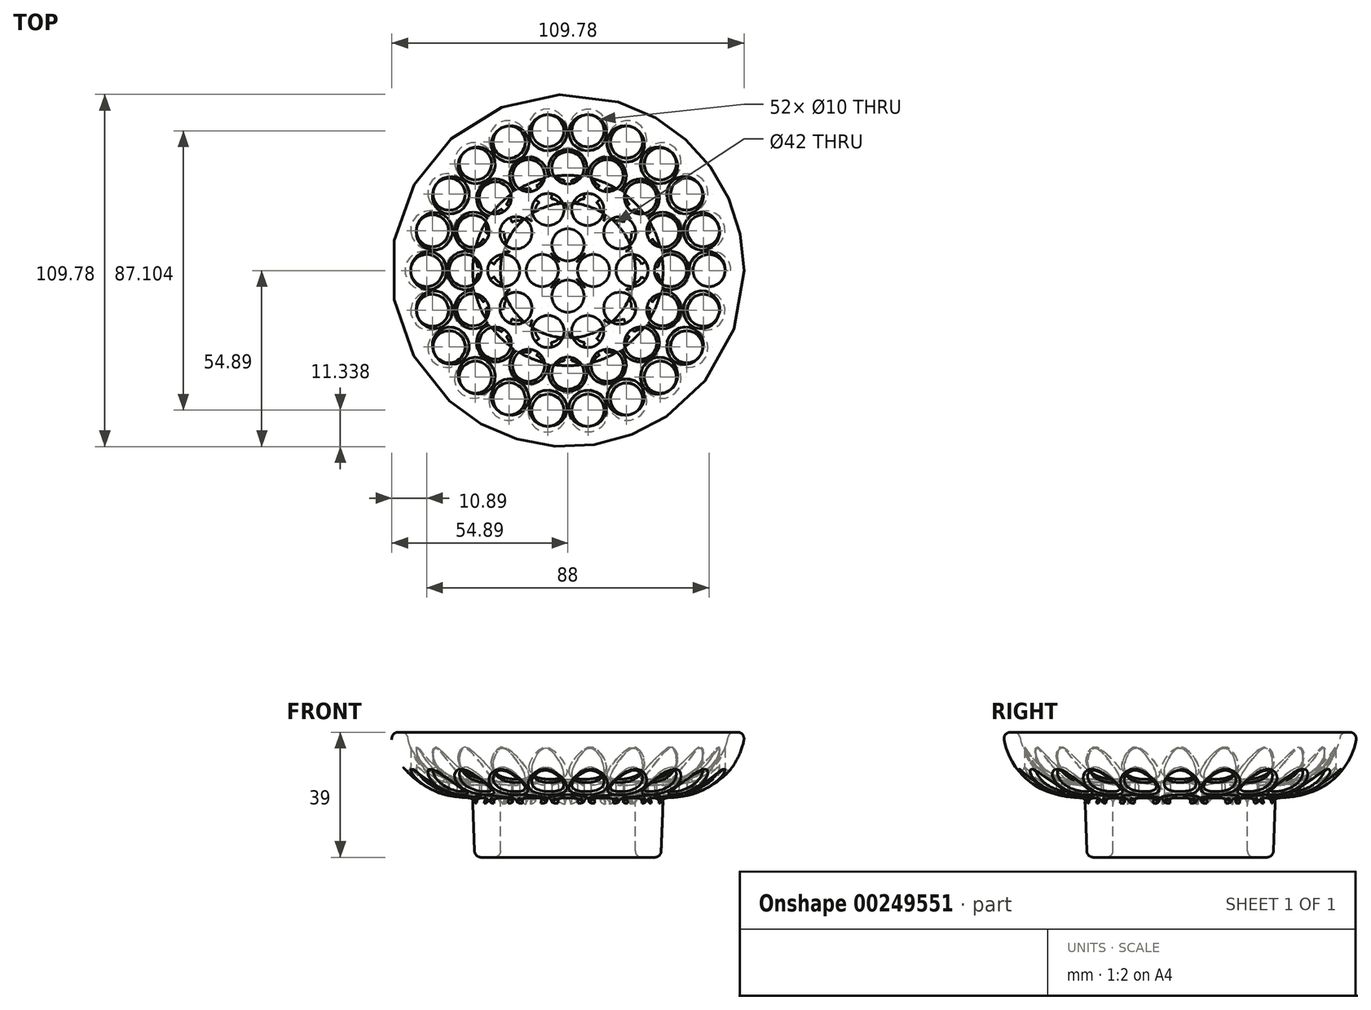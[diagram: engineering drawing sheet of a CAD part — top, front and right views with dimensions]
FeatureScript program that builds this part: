
annotation { "Feature Type Name" : "Feature", "Feature Type Description" : "" }
export const myFeature = defineFeature(function(context is Context, id is Id, definition is map)
    precondition{}
    {
        {
            var Q0;
            Q0=qCreatedBy(makeId("Front.planeOp"),FACE);
            var sketch = newSketch(context, id + "F0", { "sketchPlane" : qUnion([Q0])});
            skLineSegment(sketch, "E0", {"start": v(-23, 0) * mm, "end": v(-27.07, 0) * mm});
            skLineSegment(sketch, "E1", {"start": v(-29.07, 1.92) * mm, "end": v(-29.63, 16.62) * mm});
            skFitSpline(sketch, "E2", {"points": [v(-29.7, 18.5) * mm, v(-54.72, 35.89) * mm, v(-55, 39) * mm], "startDerivative": vector(-74.15, 0) * mm, "endDerivative": vector(0, 6.7) * mm});
            skFitSpline(sketch, "E3.0", {"points": [v(-29.7, 23.5) * mm, v(-32.43, 23.5) * mm, v(-37.07, 24.09) * mm, v(-41.99, 26.08) * mm, v(-45.41, 28.7) * mm, v(-47.75, 31.65) * mm, v(-48.95, 34.1) * mm, v(-49.55, 35.8) * mm, v(-49.78, 36.7) * mm, v(-49.9, 37.26) * mm, v(-49.97, 37.72) * mm, v(-50, 38.13) * mm, v(-50, 38.4) * mm, v(-50, 38.68) * mm, v(-50, 38.88) * mm, v(-50, 39) * mm]});
            skLineSegment(sketch, "E4", {"start": v(-52.89, 39) * mm, "end": v(-51.88, 39) * mm});
            skLineSegment(sketch, "E5", {"start": v(-29.7, 23.5) * mm, "end": v(0, 23.5) * mm});
            skLineSegment(sketch, "E6", {"start": v(0, 23.5) * mm, "end": v(0, 17.86) * mm});
            skLineSegment(sketch, "E7", {"start": v(0, 57.97) * mm, "end": v(0, -37.79) * mm, "construction": true});
            skLineSegment(sketch, "E8", {"start": v(-21, 2) * mm, "end": v(-21, 16.5) * mm});
            skLineSegment(sketch, "E9", {"start": v(-19, 18.5) * mm, "end": v(0, 18.5) * mm});
            skPoint(sketch, "E10.visualSharp", {"position": v(-21, 18.5) * mm});
            skArc(sketch, "E10.filletArc", {"start": v(-19, 18.5) * mm, "mid": v(-20.41, 17.91) * mm, "end": v(-21, 16.5) * mm});
            skPoint(sketch, "E11.visualSharp", {"position": v(-21, 0) * mm});
            skArc(sketch, "E11.filletArc", {"start": v(-23, 0) * mm, "mid": v(-21.59, 0.59) * mm, "end": v(-21, 2) * mm});
            skPoint(sketch, "E12.visualSharp", {"position": v(-29, 0) * mm});
            skArc(sketch, "E12.filletArc", {"start": v(-29.07, 1.92) * mm, "mid": v(-28.46, 0.56) * mm, "end": v(-27.07, 0) * mm});
            skArc(sketch, "E13.filletArc", {"start": v(-29.63, 16.62) * mm, "mid": v(-30.2, 17.95) * mm, "end": v(-31.54, 18.54) * mm});
            skArc(sketch, "E14.filletArc", {"start": v(-52.89, 39) * mm, "mid": v(-54.4, 38.3) * mm, "end": v(-54.87, 36.7) * mm});
            skPoint(sketch, "E15.visualSharp", {"position": v(-50, 39) * mm});
            skArc(sketch, "E15.filletArc", {"start": v(-49.9, 37.34) * mm, "mid": v(-50.59, 38.53) * mm, "end": v(-51.88, 39) * mm});
            skSolve(sketch);
        }
        {
            var Q0;
            Q0=makeQuery(id+"F0.imprint","IMPRINT",FACE,{"disambiguationData":[TD([[makeQuery(id+"F0.imprint","IMPRINT",EDGE,{"derivedFrom":sQuery(id+"F0.wireOp",EDGE,"E0")}),-1.0]])]});
            var Q1;
            Q1=sQuery(id+"F0.wireOp",EDGE,"E7");
            revolve(context, id + "F1", {"entities" : qUnion([Q0]), "axis" : qUnion([Q1]), "revolveType" : RevolveType.FULL});
        }
        {
            var Q0;
            Q0=qCreatedBy(makeId("Top.planeOp"),FACE);
            var sketch = newSketch(context, id + "F2", { "sketchPlane" : qUnion([Q0])});
            skCircle(sketch, "E16", {"center": v(-8, 0) * mm, "radius": 5 * mm});
            skCircle(sketch, "E17.1.0.0", {"center": v(-20, 0) * mm, "radius": 5 * mm});
            skCircle(sketch, "E17.2.0.0", {"center": v(-32, 0) * mm, "radius": 5 * mm});
            skCircle(sketch, "E17.3.0.0", {"center": v(-44, 0) * mm, "radius": 5 * mm});
            skLineSegment(sketch, "E17.direction1", {"start": v(-8, 0) * mm, "end": v(-20, 0) * mm, "construction": true});
            skCircle(sketch, "E18.1.0", {"center": v(-42.22, -12.4) * mm, "radius": 5 * mm});
            skCircle(sketch, "E18.2.0", {"center": v(-37.02, -23.79) * mm, "radius": 5 * mm});
            skCircle(sketch, "E18.3.0", {"center": v(-28.81, -33.25) * mm, "radius": 5 * mm});
            skCircle(sketch, "E18.4.0", {"center": v(-18.28, -40.02) * mm, "radius": 5 * mm});
            skCircle(sketch, "E18.5.0", {"center": v(-6.26, -43.55) * mm, "radius": 5 * mm});
            skCircle(sketch, "E18.6.0", {"center": v(6.26, -43.55) * mm, "radius": 5 * mm});
            skCircle(sketch, "E18.7.0", {"center": v(18.28, -40.02) * mm, "radius": 5 * mm});
            skCircle(sketch, "E18.8.0", {"center": v(28.81, -33.25) * mm, "radius": 5 * mm});
            skCircle(sketch, "E18.9.0", {"center": v(37.02, -23.79) * mm, "radius": 5 * mm});
            skCircle(sketch, "E18.10.0", {"center": v(42.22, -12.4) * mm, "radius": 5 * mm});
            skCircle(sketch, "E18.11.0", {"center": v(44, 0) * mm, "radius": 5 * mm});
            skCircle(sketch, "E18.12.0", {"center": v(42.22, 12.4) * mm, "radius": 5 * mm});
            skCircle(sketch, "E18.13.0", {"center": v(37.02, 23.79) * mm, "radius": 5 * mm});
            skCircle(sketch, "E18.14.0", {"center": v(28.81, 33.25) * mm, "radius": 5 * mm});
            skCircle(sketch, "E18.15.0", {"center": v(18.28, 40.02) * mm, "radius": 5 * mm});
            skCircle(sketch, "E18.16.0", {"center": v(6.26, 43.55) * mm, "radius": 5 * mm});
            skCircle(sketch, "E18.17.0", {"center": v(-6.26, 43.55) * mm, "radius": 5 * mm});
            skCircle(sketch, "E18.18.0", {"center": v(-18.28, 40.02) * mm, "radius": 5 * mm});
            skCircle(sketch, "E18.19.0", {"center": v(-28.81, 33.25) * mm, "radius": 5 * mm});
            skCircle(sketch, "E18.20.0", {"center": v(-37.02, 23.79) * mm, "radius": 5 * mm});
            skCircle(sketch, "E18.21.0", {"center": v(-42.22, 12.4) * mm, "radius": 5 * mm});
            skPoint(sketch, "E18.center", {"position": v(0, 0) * mm});
            skCircle(sketch, "E19.1.0", {"center": v(-29.56, -12.25) * mm, "radius": 5 * mm});
            skCircle(sketch, "E19.2.0", {"center": v(-22.63, -22.63) * mm, "radius": 5 * mm});
            skCircle(sketch, "E19.3.0", {"center": v(-12.25, -29.56) * mm, "radius": 5 * mm});
            skCircle(sketch, "E19.4.0", {"center": v(0, -32) * mm, "radius": 5 * mm});
            skCircle(sketch, "E19.5.0", {"center": v(12.25, -29.56) * mm, "radius": 5 * mm});
            skCircle(sketch, "E19.6.0", {"center": v(22.63, -22.63) * mm, "radius": 5 * mm});
            skCircle(sketch, "E19.7.0", {"center": v(29.56, -12.25) * mm, "radius": 5 * mm});
            skCircle(sketch, "E19.8.0", {"center": v(32, 0) * mm, "radius": 5 * mm});
            skCircle(sketch, "E19.9.0", {"center": v(29.56, 12.25) * mm, "radius": 5 * mm});
            skCircle(sketch, "E19.10.0", {"center": v(22.63, 22.63) * mm, "radius": 5 * mm});
            skCircle(sketch, "E19.11.0", {"center": v(12.25, 29.56) * mm, "radius": 5 * mm});
            skCircle(sketch, "E19.12.0", {"center": v(0, 32) * mm, "radius": 5 * mm});
            skCircle(sketch, "E19.13.0", {"center": v(-12.25, 29.56) * mm, "radius": 5 * mm});
            skCircle(sketch, "E19.14.0", {"center": v(-22.63, 22.63) * mm, "radius": 5 * mm});
            skCircle(sketch, "E19.15.0", {"center": v(-29.56, 12.25) * mm, "radius": 5 * mm});
            skCircle(sketch, "E20.1.0", {"center": v(-16.18, -11.76) * mm, "radius": 5 * mm});
            skCircle(sketch, "E20.2.0", {"center": v(-6.18, -19.02) * mm, "radius": 5 * mm});
            skCircle(sketch, "E20.3.0", {"center": v(6.18, -19.02) * mm, "radius": 5 * mm});
            skCircle(sketch, "E20.4.0", {"center": v(16.18, -11.76) * mm, "radius": 5 * mm});
            skCircle(sketch, "E20.5.0", {"center": v(20, 0) * mm, "radius": 5 * mm});
            skCircle(sketch, "E20.6.0", {"center": v(16.18, 11.76) * mm, "radius": 5 * mm});
            skCircle(sketch, "E20.7.0", {"center": v(6.18, 19.02) * mm, "radius": 5 * mm});
            skCircle(sketch, "E20.8.0", {"center": v(-6.18, 19.02) * mm, "radius": 5 * mm});
            skCircle(sketch, "E20.9.0", {"center": v(-16.18, 11.76) * mm, "radius": 5 * mm});
            skCircle(sketch, "E21.1.0", {"center": v(0, -8) * mm, "radius": 5 * mm});
            skCircle(sketch, "E21.2.0", {"center": v(8, 0) * mm, "radius": 5 * mm});
            skCircle(sketch, "E21.3.0", {"center": v(0, 8) * mm, "radius": 5 * mm});
            skSolve(sketch);
        }
        {
            var Q0;
            Q0=qSketchRegion(id+"F2",true);
            extrude(context, id + "F3", {"entities" : qUnion([Q0]), "operationType" : NewBodyOperationType.REMOVE, "depth" : 40 * mm, "hasSecondDirection" : true, "secondDirectionOppositeDirection" : false, "secondDirectionDepth" : 18.5 * mm});
        }
        {
            var Q0;
            Q0=makeQuery(id+"F1.opRevolve","SWEPT_FACE",FACE,{"disambiguationData":[OSD([sQuery(id+"F0.wireOp",EDGE,"E3.0")])]});
            var Q1;
            Q1=makeQuery(id+"F1.opRevolve","SWEPT_FACE",FACE,{"disambiguationData":[OSD([sQuery(id+"F0.wireOp",EDGE,"E5")])]});
            var Q2;
            Q2=makeQuery(id+"F1.opRevolve","SWEPT_FACE",FACE,{"disambiguationData":[OSD([sQuery(id+"F0.wireOp",EDGE,"E9")])]});
            var Q3;
            Q3=makeQuery(id+"F1.opRevolve","SWEPT_FACE",FACE,{"disambiguationData":[OSD([sQuery(id+"F0.wireOp",EDGE,"E2")])]});
            fillet(context, id + "F4", {"entities" : qUnion([Q0, Q1, Q2, Q3]), "radius" : 1 * mm, "tangentPropagation" : true, "allowEdgeOverflow" : false});
        }
        {
            var Q0;
            Q0=makeQuery(id+"F1.opRevolve","SWEPT_FACE",FACE,{"disambiguationData":[OSD([sQuery(id+"F0.wireOp",EDGE,"E13.filletArc")])]});
            fillet(context, id + "F5", {"entities" : qUnion([Q0]), "radius" : 1.5 * mm, "tangentPropagation" : true, "allowEdgeOverflow" : false});
        }
        {
            var Q0;
            Q0=makeQuery(id+"F1.opRevolve","SWEPT_FACE",FACE,{"disambiguationData":[OSD([sQuery(id+"F0.wireOp",EDGE,"E10.filletArc")])]});
            fillet(context, id + "F6", {"entities" : qUnion([Q0]), "radius" : 2 * mm, "tangentPropagation" : true, "allowEdgeOverflow" : false});
        }
        {
            var Q0;
            Q0=makeQuery(id+"F3.boolean.opBoolean","COPY",EDGE,{"derivedFrom":makeQuery(id+"F3.opExtrude","CAP_EDGE",EDGE,{"disambiguationData":[OSD([sQuery(id+"F2.wireOp",EDGE,"E19.3.0")])],"isStart":true})});
            var Q1;
            Q1=makeQuery(id+"F3.boolean.opBoolean","COPY",EDGE,{"derivedFrom":makeQuery(id+"F3.opExtrude","CAP_EDGE",EDGE,{"disambiguationData":[OSD([sQuery(id+"F2.wireOp",EDGE,"E19.4.0")])],"isStart":true})});
            var Q2;
            Q2=makeQuery(id+"F3.boolean.opBoolean","COPY",EDGE,{"derivedFrom":makeQuery(id+"F3.opExtrude","CAP_EDGE",EDGE,{"disambiguationData":[OSD([sQuery(id+"F2.wireOp",EDGE,"E19.5.0")])],"isStart":true})});
            var Q3;
            Q3=makeQuery(id+"F3.boolean.opBoolean","COPY",EDGE,{"derivedFrom":makeQuery(id+"F3.opExtrude","CAP_EDGE",EDGE,{"disambiguationData":[OSD([sQuery(id+"F2.wireOp",EDGE,"E19.6.0")])],"isStart":true})});
            var Q4;
            Q4=makeQuery(id+"F3.boolean.opBoolean","COPY",EDGE,{"derivedFrom":makeQuery(id+"F3.opExtrude","CAP_EDGE",EDGE,{"disambiguationData":[OSD([sQuery(id+"F2.wireOp",EDGE,"E19.7.0")])],"isStart":true})});
            var Q5;
            Q5=makeQuery(id+"F3.boolean.opBoolean","COPY",EDGE,{"derivedFrom":makeQuery(id+"F3.opExtrude","CAP_EDGE",EDGE,{"disambiguationData":[OSD([sQuery(id+"F2.wireOp",EDGE,"E19.8.0")])],"isStart":true})});
            var Q6;
            Q6=makeQuery(id+"F3.boolean.opBoolean","COPY",EDGE,{"derivedFrom":makeQuery(id+"F3.opExtrude","CAP_EDGE",EDGE,{"disambiguationData":[OSD([sQuery(id+"F2.wireOp",EDGE,"E19.9.0")])],"isStart":true})});
            var Q7;
            Q7=makeQuery(id+"F3.boolean.opBoolean","COPY",EDGE,{"derivedFrom":makeQuery(id+"F3.opExtrude","CAP_EDGE",EDGE,{"disambiguationData":[OSD([sQuery(id+"F2.wireOp",EDGE,"E19.10.0")])],"isStart":true})});
            var Q8;
            Q8=makeQuery(id+"F3.boolean.opBoolean","COPY",EDGE,{"derivedFrom":makeQuery(id+"F3.opExtrude","CAP_EDGE",EDGE,{"disambiguationData":[OSD([sQuery(id+"F2.wireOp",EDGE,"E19.11.0")])],"isStart":true})});
            var Q9;
            Q9=makeQuery(id+"F3.boolean.opBoolean","COPY",EDGE,{"derivedFrom":makeQuery(id+"F3.opExtrude","CAP_EDGE",EDGE,{"disambiguationData":[OSD([sQuery(id+"F2.wireOp",EDGE,"E19.12.0")])],"isStart":true})});
            var Q10;
            Q10=makeQuery(id+"F3.boolean.opBoolean","COPY",EDGE,{"derivedFrom":makeQuery(id+"F3.opExtrude","CAP_EDGE",EDGE,{"disambiguationData":[OSD([sQuery(id+"F2.wireOp",EDGE,"E19.13.0")])],"isStart":true})});
            var Q11;
            Q11=makeQuery(id+"F3.boolean.opBoolean","COPY",EDGE,{"derivedFrom":makeQuery(id+"F3.opExtrude","CAP_EDGE",EDGE,{"disambiguationData":[OSD([sQuery(id+"F2.wireOp",EDGE,"E19.14.0")])],"isStart":true})});
            var Q12;
            Q12=makeQuery(id+"F3.boolean.opBoolean","COPY",EDGE,{"derivedFrom":makeQuery(id+"F3.opExtrude","CAP_EDGE",EDGE,{"disambiguationData":[OSD([sQuery(id+"F2.wireOp",EDGE,"E19.15.0")])],"isStart":true})});
            var Q13;
            Q13=makeQuery(id+"F3.boolean.opBoolean","COPY",EDGE,{"derivedFrom":makeQuery(id+"F3.opExtrude","CAP_EDGE",EDGE,{"disambiguationData":[OSD([sQuery(id+"F2.wireOp",EDGE,"E17.2.0.0")])],"isStart":true})});
            var Q14;
            Q14=makeQuery(id+"F3.boolean.opBoolean","COPY",EDGE,{"derivedFrom":makeQuery(id+"F3.opExtrude","CAP_EDGE",EDGE,{"disambiguationData":[OSD([sQuery(id+"F2.wireOp",EDGE,"E19.1.0")])],"isStart":true})});
            var Q15;
            Q15=makeQuery(id+"F3.boolean.opBoolean","COPY",EDGE,{"derivedFrom":makeQuery(id+"F3.opExtrude","CAP_EDGE",EDGE,{"disambiguationData":[OSD([sQuery(id+"F2.wireOp",EDGE,"E19.2.0")])],"isStart":true})});
            fillet(context, id + "F7", {"entities" : qUnion([Q0, Q1, Q2, Q3, Q4, Q5, Q6, Q7, Q8, Q9, Q10, Q11, Q12, Q13, Q14, Q15]), "radius" : 1 * mm, "tangentPropagation" : true, "allowEdgeOverflow" : false});
        }
        {
            var Q0;
            Q0=makeQuery(id+"F3.boolean.opBoolean","COPY",EDGE,{"disambiguationData":[OD(0.0)],"derivedFrom":makeQuery(id+"F3.opExtrude","CAP_EDGE",EDGE,{"disambiguationData":[OSD([sQuery(id+"F2.wireOp",EDGE,"E20.3.0")])],"isStart":true})});
            var Q1;
            Q1=makeQuery(id+"F3.boolean.opBoolean","COPY",EDGE,{"disambiguationData":[OD(0.0)],"derivedFrom":makeQuery(id+"F3.opExtrude","CAP_EDGE",EDGE,{"disambiguationData":[OSD([sQuery(id+"F2.wireOp",EDGE,"E20.4.0")])],"isStart":true})});
            var Q2;
            Q2=makeQuery(id+"F3.boolean.opBoolean","COPY",EDGE,{"disambiguationData":[OD(0.0)],"derivedFrom":makeQuery(id+"F3.opExtrude","CAP_EDGE",EDGE,{"disambiguationData":[OSD([sQuery(id+"F2.wireOp",EDGE,"E20.5.0")])],"isStart":true})});
            var Q3;
            Q3=makeQuery(id+"F3.boolean.opBoolean","COPY",EDGE,{"disambiguationData":[OD(0.0)],"derivedFrom":makeQuery(id+"F3.opExtrude","CAP_EDGE",EDGE,{"disambiguationData":[OSD([sQuery(id+"F2.wireOp",EDGE,"E20.6.0")])],"isStart":true})});
            var Q4;
            Q4=makeQuery(id+"F3.boolean.opBoolean","COPY",EDGE,{"disambiguationData":[OD(0.0)],"derivedFrom":makeQuery(id+"F3.opExtrude","CAP_EDGE",EDGE,{"disambiguationData":[OSD([sQuery(id+"F2.wireOp",EDGE,"E20.7.0")])],"isStart":true})});
            var Q5;
            Q5=makeQuery(id+"F3.boolean.opBoolean","COPY",EDGE,{"disambiguationData":[OD(0.0)],"derivedFrom":makeQuery(id+"F3.opExtrude","CAP_EDGE",EDGE,{"disambiguationData":[OSD([sQuery(id+"F2.wireOp",EDGE,"E20.8.0")])],"isStart":true})});
            var Q6;
            Q6=makeQuery(id+"F3.boolean.opBoolean","COPY",EDGE,{"disambiguationData":[OD(0.0)],"derivedFrom":makeQuery(id+"F3.opExtrude","CAP_EDGE",EDGE,{"disambiguationData":[OSD([sQuery(id+"F2.wireOp",EDGE,"E20.9.0")])],"isStart":true})});
            var Q7;
            Q7=makeQuery(id+"F3.boolean.opBoolean","COPY",EDGE,{"disambiguationData":[OD(0.0)],"derivedFrom":makeQuery(id+"F3.opExtrude","CAP_EDGE",EDGE,{"disambiguationData":[OSD([sQuery(id+"F2.wireOp",EDGE,"E20.1.0")])],"isStart":true})});
            var Q8;
            Q8=makeQuery(id+"F3.boolean.opBoolean","COPY",EDGE,{"disambiguationData":[OD(0.0)],"derivedFrom":makeQuery(id+"F3.opExtrude","CAP_EDGE",EDGE,{"disambiguationData":[OSD([sQuery(id+"F2.wireOp",EDGE,"E20.2.0")])],"isStart":true})});
            var Q9;
            Q9=makeQuery(id+"F3.boolean.opBoolean","COPY",EDGE,{"disambiguationData":[OD(0.0)],"derivedFrom":makeQuery(id+"F3.opExtrude","CAP_EDGE",EDGE,{"disambiguationData":[OSD([sQuery(id+"F2.wireOp",EDGE,"E17.1.0.0")])],"isStart":true})});
            fillet(context, id + "F8", {"entities" : qUnion([Q0, Q1, Q2, Q3, Q4, Q5, Q6, Q7, Q8, Q9]), "radius" : 1.5 * mm, "tangentPropagation" : true, "allowEdgeOverflow" : false});
        }
    });
